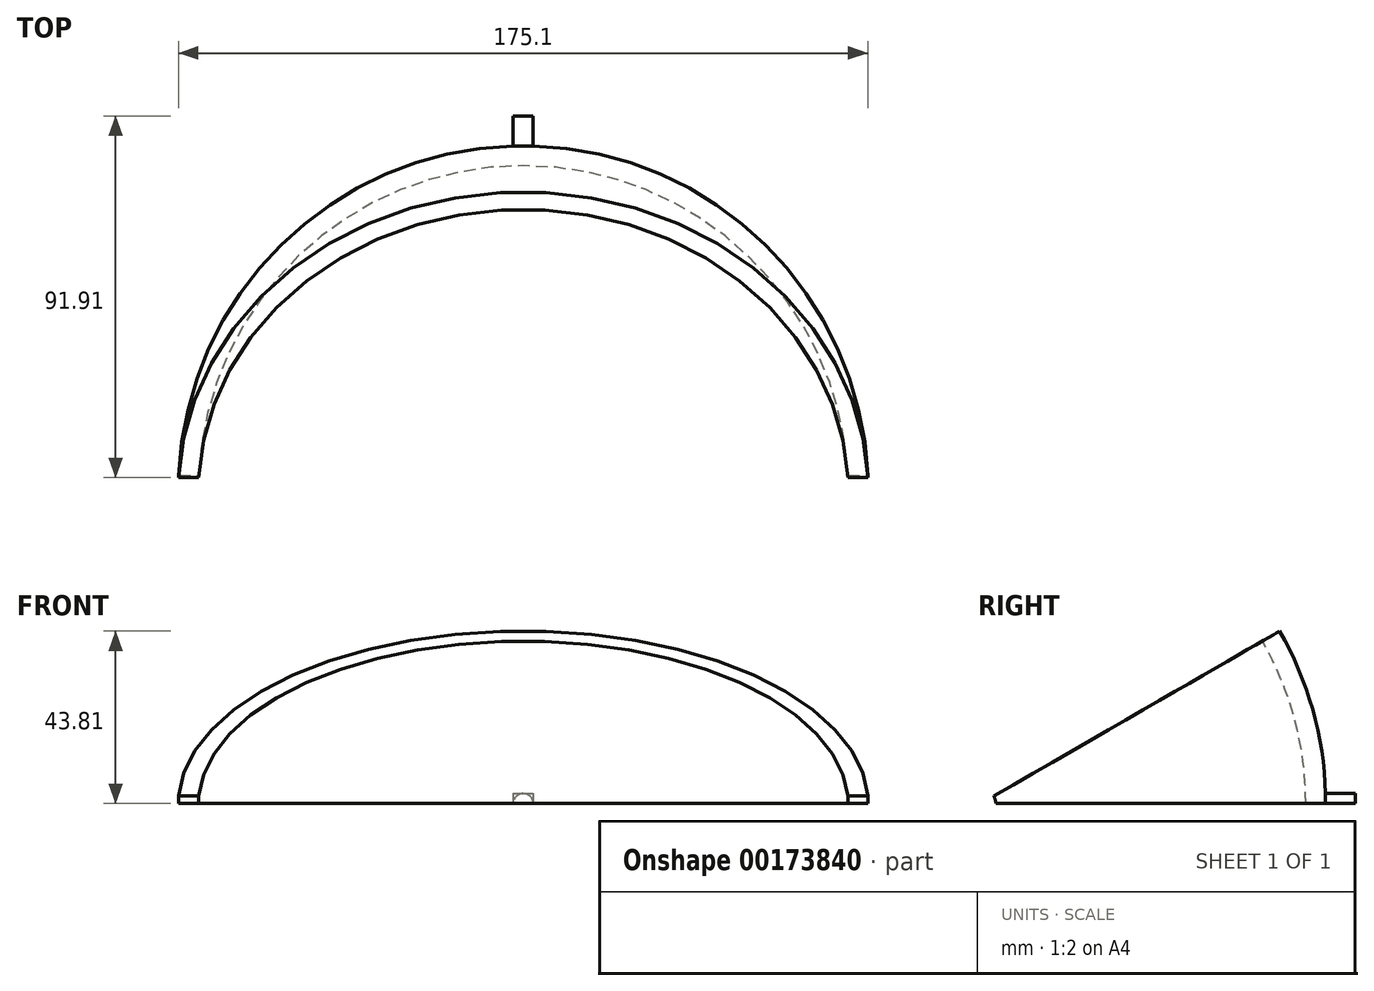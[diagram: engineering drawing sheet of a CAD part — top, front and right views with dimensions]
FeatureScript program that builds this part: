
annotation { "Feature Type Name" : "Feature", "Feature Type Description" : "" }
export const myFeature = defineFeature(function(context is Context, id is Id, definition is map)
    precondition{}
    {
        {
            var Q0;
            Q0=qCreatedBy(makeId("Top.planeOp"),FACE);
            var sketch = newSketch(context, id + "F0", { "sketchPlane" : qUnion([Q0])});
            skLineSegment(sketch, "E0", {"start": v(0, 0) * mm, "end": v(-82.55, 0) * mm, "construction": true});
            skArc(sketch, "E1", {"start": v(-82.55, 0) * mm, "mid": v(0, 82.55) * mm, "end": v(82.55, 0) * mm});
            skLineSegment(sketch, "E2", {"start": v(-82.55, 0) * mm, "end": v(-87.63, 0) * mm});
            skArc(sketch, "E3", {"start": v(-87.63, 0) * mm, "mid": v(0, 87.63) * mm, "end": v(87.63, 0) * mm});
            skLineSegment(sketch, "E4", {"start": v(82.55, 0) * mm, "end": v(-82.55, 0) * mm, "construction": true});
            skLineSegment(sketch, "E5", {"start": v(82.55, 0) * mm, "end": v(87.63, 0) * mm});
            skSolve(sketch);
        }
        {
            var Q0;
            Q0 = qSketchRegion(id + "F0", true);
            var Q1;
            Q1=sQuery(id+"F0.wireOp",EDGE,"E0");
            revolve(context, id + "F1", {"entities" : qUnion([Q0]), "axis" : qUnion([Q1]), "revolveType" : RevolveType.ONE_DIRECTION, "oppositeDirection" : true, "angle" : 30 * degree});
        }
        {
            var Q0;
            Q0=qCreatedBy(makeId("Right.planeOp"),FACE);
            var sketch = newSketch(context, id + "F2", { "sketchPlane" : qUnion([Q0])});
            skCircle(sketch, "E6", {"center": v(0, 0) * mm, "radius": 3.81 * mm});
            skSolve(sketch);
        }
        {
            var Q0;
            Q0 = qSketchRegion(id + "F2", true);
            extrude(context, id + "F3", {"entities" : qUnion([Q0]), "operationType" : NewBodyOperationType.REMOVE, "endBound" : BoundingType.THROUGH_ALL, "oppositeDirection" : true, "depth" : 25.4 * mm, "hasSecondDirection" : true, "secondDirectionBound" : SecondDirectionBoundingType.THROUGH_ALL, "secondDirectionOppositeDirection" : false, "secondDirectionDepth" : 25.4 * mm});
        }
        {
            var Q0;
            Q0=qCreatedBy(makeId("Top.planeOp"),FACE);
            var sketch = newSketch(context, id + "F4", { "sketchPlane" : qUnion([Q0])});
            skLineSegment(sketch, "E7", {"start": v(0, 0) * mm, "end": v(2.54, 0) * mm, "construction": true});
            skLineSegment(sketch, "E8", {"start": v(0, 0) * mm, "end": v(-2.54, 0) * mm, "construction": true});
            skLineSegment(sketch, "E9", {"start": v(0, 0) * mm, "end": v(-82.55, 0) * mm, "construction": true});
            skLineSegment(sketch, "E10", {"start": v(0, 0) * mm, "end": v(-87.63, 0) * mm, "construction": true});
            skLineSegment(sketch, "E11", {"start": v(-2.54, 95.21) * mm, "end": v(2.54, 95.21) * mm});
            skArc(sketch, "E12", {"start": v(-82.55, 0) * mm, "mid": v(0, 82.55) * mm, "end": v(82.55, 0) * mm, "construction": true});
            skLineSegment(sketch, "E13", {"start": v(-2.54, 101.6) * mm, "end": v(-2.54, 0) * mm, "construction": true});
            skLineSegment(sketch, "E14", {"start": v(2.54, 0) * mm, "end": v(2.54, 101.6) * mm, "construction": true});
            skLineSegment(sketch, "E15", {"start": v(-2.54, 87.6) * mm, "end": v(-2.54, 95.21) * mm});
            skLineSegment(sketch, "E16", {"start": v(2.54, 87.6) * mm, "end": v(2.54, 95.21) * mm});
            skLineSegment(sketch, "E17", {"start": v(-2.54, 87.6) * mm, "end": v(2.54, 87.6) * mm});
            skSolve(sketch);
        }
        {
            var Q0;
            Q0=makeQuery(id+"F4.imprint","IMPRINT",FACE,{"disambiguationData":[TD([[makeQuery(id+"F4.imprint","IMPRINT",EDGE,{"derivedFrom":sQuery(id+"F4.wireOp",EDGE,"E11")}),-1.0]])]});
            extrude(context, id + "F5", {"entities" : qUnion([Q0]), "operationType" : NewBodyOperationType.ADD, "depth" : 2.54 * mm});
        }
    });
